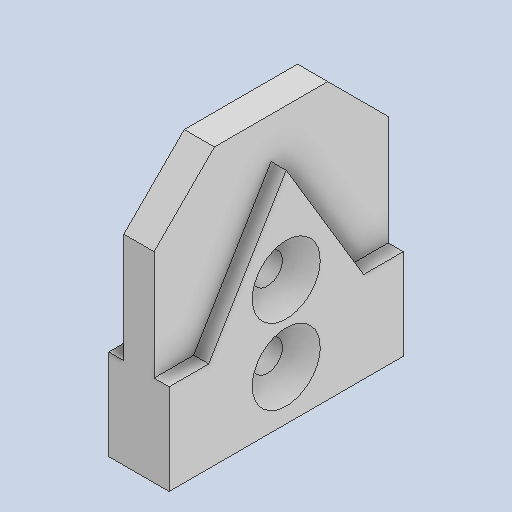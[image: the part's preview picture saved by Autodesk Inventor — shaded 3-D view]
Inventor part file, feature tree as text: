
AUTODESK INVENTOR PART (.ipt)
format: ipt  version: 2022 (Build 260153000, 153)  size: 146,432 bytes
history: native  units: in
note: dims shown in document units (in); Inventor stores cm internally (conversion verified against a paired STEP export)
features: sketch x5, other x3
ambient origin geometry x8: Origin, YZ Plane, XZ Plane, XY Plane, X Axis, Y Axis, Z Axis, Center Point
bodies: Solid1 (feature_tree)
feature tree (8):
  other  "Traingular Hopper Connector.ipt"
  other  "Solid1::Traingular Hopper Connector.ipt"
  other  "TaggingFeature1"
  sketch  "Sketch1"  dims[d0=0.3937in]
  sketch  "Sketch2"
  sketch  "Sketch7"
  sketch  "Sketch8"
  sketch  "Sketch9"
